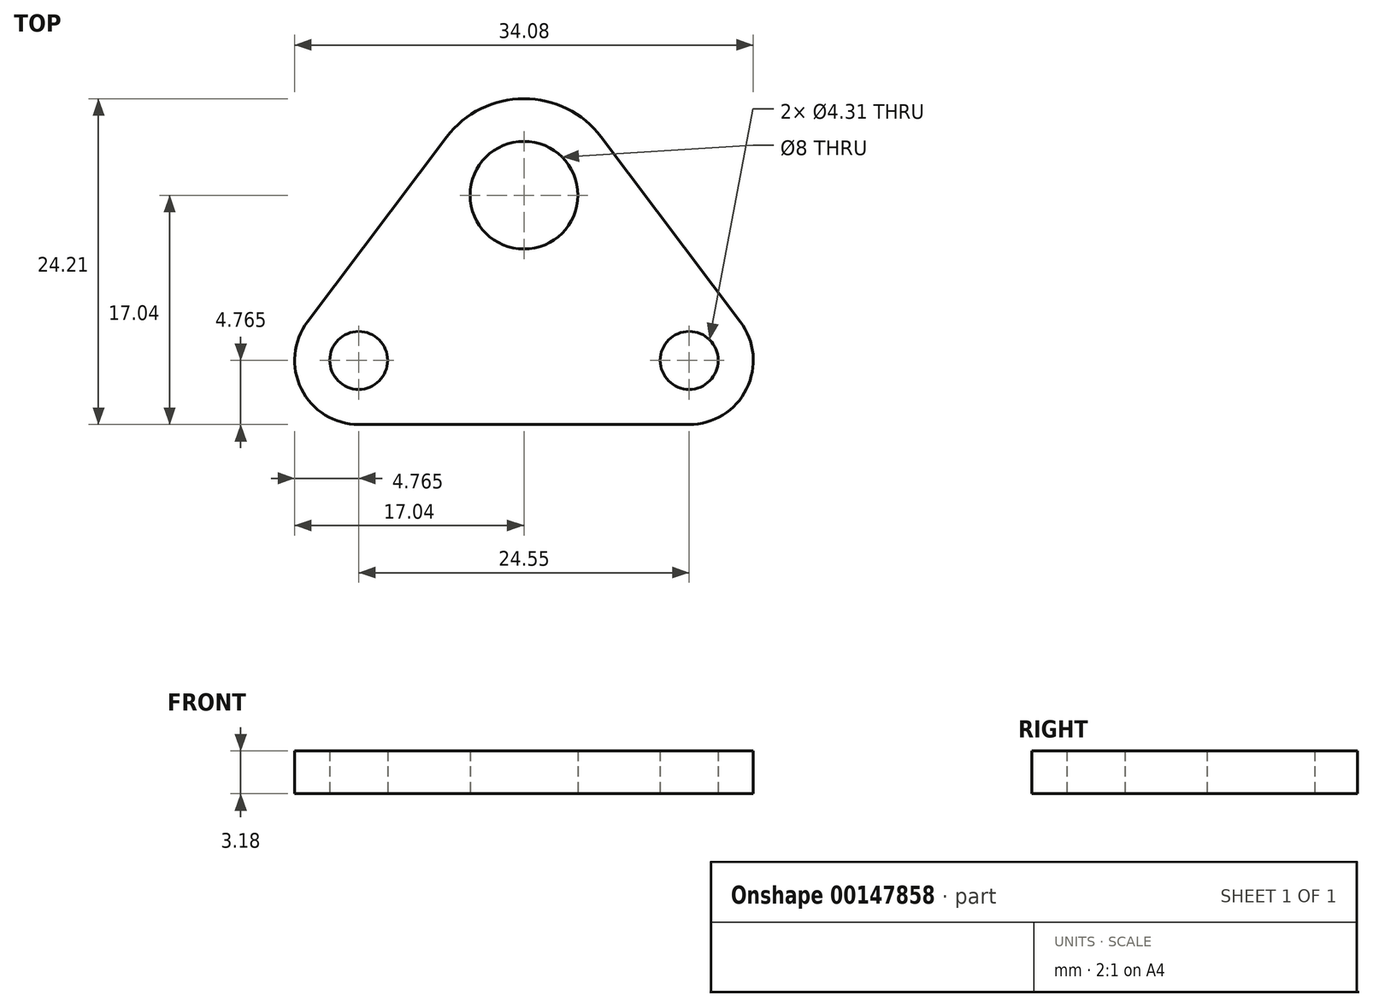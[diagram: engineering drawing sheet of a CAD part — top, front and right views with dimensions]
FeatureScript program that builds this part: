
annotation { "Feature Type Name" : "Feature", "Feature Type Description" : "" }
export const myFeature = defineFeature(function(context is Context, id is Id, definition is map)
    precondition{}
    {
        {
            var Q0;
            Q0=qCreatedBy(makeId("Top.planeOp"),FACE);
            var sketch = newSketch(context, id + "F0", { "sketchPlane" : qUnion([Q0])});
            skCircle(sketch, "E0", {"center": v(0, 0) * mm, "radius": 4 * mm});
            skArc(sketch, "E1", {"start": v(5.73, 4.32) * mm, "mid": v(0, 7.18) * mm, "end": v(-5.73, 4.32) * mm});
            skLineSegment(sketch, "E2", {"start": v(5.73, 4.32) * mm, "end": v(16.08, -9.4) * mm});
            skLineSegment(sketch, "E3", {"start": v(-5.73, 4.32) * mm, "end": v(-16.08, -9.4) * mm});
            skLineSegment(sketch, "E4", {"start": v(0, 0) * mm, "end": v(0, -12.28) * mm, "construction": true});
            skLineSegment(sketch, "E5", {"start": v(-12.28, -12.28) * mm, "end": v(12.28, -12.28) * mm, "construction": true});
            skLineSegment(sketch, "E6", {"start": v(-12.28, -17.04) * mm, "end": v(12.28, -17.04) * mm});
            skArc(sketch, "E7", {"start": v(-16.08, -9.4) * mm, "mid": v(-16.54, -14.4) * mm, "end": v(-12.28, -17.04) * mm});
            skArc(sketch, "E8", {"start": v(12.28, -17.04) * mm, "mid": v(16.54, -14.4) * mm, "end": v(16.08, -9.4) * mm});
            skCircle(sketch, "E9", {"center": v(-12.28, -12.28) * mm, "radius": 2.15 * mm});
            skCircle(sketch, "E10", {"center": v(12.28, -12.28) * mm, "radius": 2.15 * mm});
            skArc(sketch, "E11", {"start": v(16.08, -9.4) * mm, "mid": v(8.01, -10.15) * mm, "end": v(12.28, -17.04) * mm, "construction": true});
            skCircle(sketch, "E12", {"center": v(0, 0) * mm, "radius": 12.6 * mm, "construction": true});
            skLineSegment(sketch, "E13", {"start": v(0, 0) * mm, "end": v(12.28, -12.28) * mm, "construction": true});
            skSolve(sketch);
        }
        {
            var Q0;
            Q0=qSketchRegion(id+"F0",true);
            extrude(context, id + "F1", {"entities" : qUnion([Q0]), "depth" : 3.17 * mm});
        }
    });
